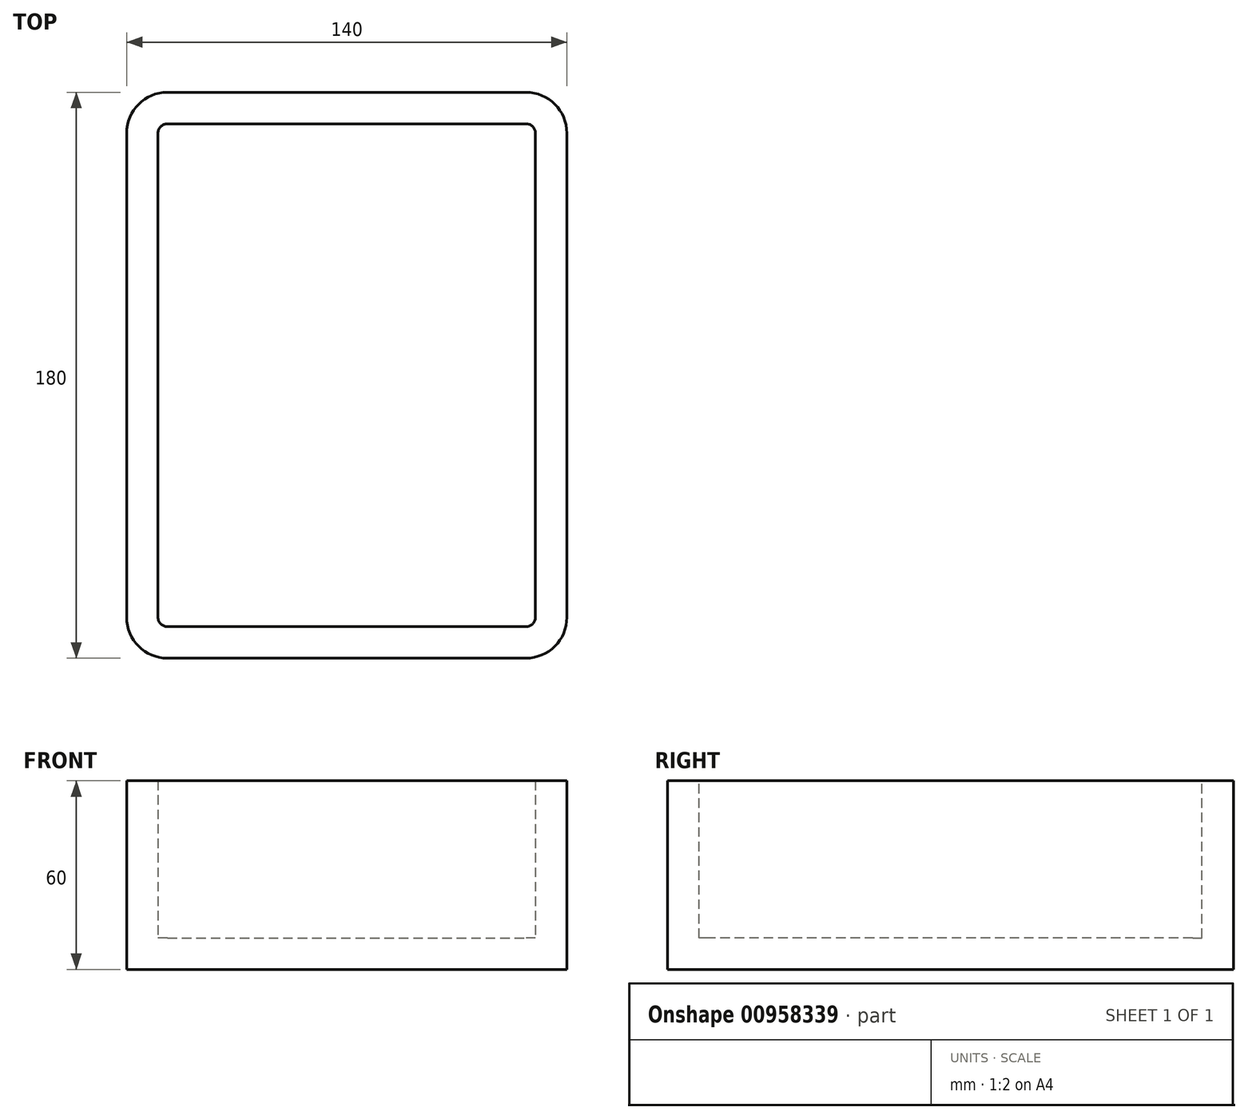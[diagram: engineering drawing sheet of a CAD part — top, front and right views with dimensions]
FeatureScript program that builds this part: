
annotation { "Feature Type Name" : "Feature", "Feature Type Description" : "" }
export const myFeature = defineFeature(function(context is Context, id is Id, definition is map)
    precondition{}
    {
        {
            var Q0;
            Q0=qCreatedBy(makeId("Top.planeOp"),FACE);
            var sketch = newSketch(context, id + "F0", { "sketchPlane" : qUnion([Q0])});
            skLineSegment(sketch, "E0.bottom", {"start": v(-23.2, 133.48) * mm, "end": v(116.8, 133.48) * mm});
            skLineSegment(sketch, "E0.top", {"start": v(-23.2, -46.52) * mm, "end": v(116.8, -46.52) * mm});
            skLineSegment(sketch, "E0.left", {"start": v(-23.2, 133.48) * mm, "end": v(-23.2, -46.52) * mm});
            skLineSegment(sketch, "E0.right", {"start": v(116.8, 133.48) * mm, "end": v(116.8, -46.52) * mm});
            skSolve(sketch);
        }
        {
            var Q0;
            Q0=makeQuery(id+"F0.imprint","IMPRINT",FACE,{"disambiguationData":[TD([[makeQuery(id+"F0.imprint","IMPRINT",EDGE,{"derivedFrom":sQuery(id+"F0.wireOp",EDGE,"E0.bottom")}),-1.0]])]});
            extrude(context, id + "F1", {"entities" : qUnion([Q0]), "depth" : 60 * mm, "offsetDistance" : 25 * mm});
        }
        {
            var Q0;
            Q0=makeQuery(id+"F1.opExtrude","SWEPT_EDGE",EDGE,{"disambiguationData":[OSD([sQuery(id+"F0.wireOp",EDGE,"E0.bottom"),sQuery(id+"F0.wireOp",EDGE,"E0.left")])]});
            var Q1;
            Q1=makeQuery(id+"F1.opExtrude","SWEPT_EDGE",EDGE,{"disambiguationData":[OSD([sQuery(id+"F0.wireOp",EDGE,"E0.bottom"),sQuery(id+"F0.wireOp",EDGE,"E0.right")])]});
            var Q2;
            Q2=makeQuery(id+"F1.opExtrude","SWEPT_EDGE",EDGE,{"disambiguationData":[OSD([sQuery(id+"F0.wireOp",EDGE,"E0.top"),sQuery(id+"F0.wireOp",EDGE,"E0.left")])]});
            var Q3;
            Q3=makeQuery(id+"F1.opExtrude","SWEPT_EDGE",EDGE,{"disambiguationData":[OSD([sQuery(id+"F0.wireOp",EDGE,"E0.top"),sQuery(id+"F0.wireOp",EDGE,"E0.right")])]});
            fillet(context, id + "F2", {"entities" : qUnion([Q0, Q1, Q2, Q3]), "radius" : 13 * mm, "tangentPropagation" : true, "allowEdgeOverflow" : false});
        }
        {
            var Q0;
            Q0=makeQuery(id+"F1.opExtrude","CAP_FACE",FACE,{"disambiguationData":[OSD([sQuery(id+"F0.wireOp",EDGE,"E0.bottom"),sQuery(id+"F0.wireOp",EDGE,"E0.top"),sQuery(id+"F0.wireOp",EDGE,"E0.left"),sQuery(id+"F0.wireOp",EDGE,"E0.right")])],"isStart":false});
            shell(context, id + "F3", {"entities" : qUnion([Q0]), "thickness" : 10 * mm});
        }
    });
